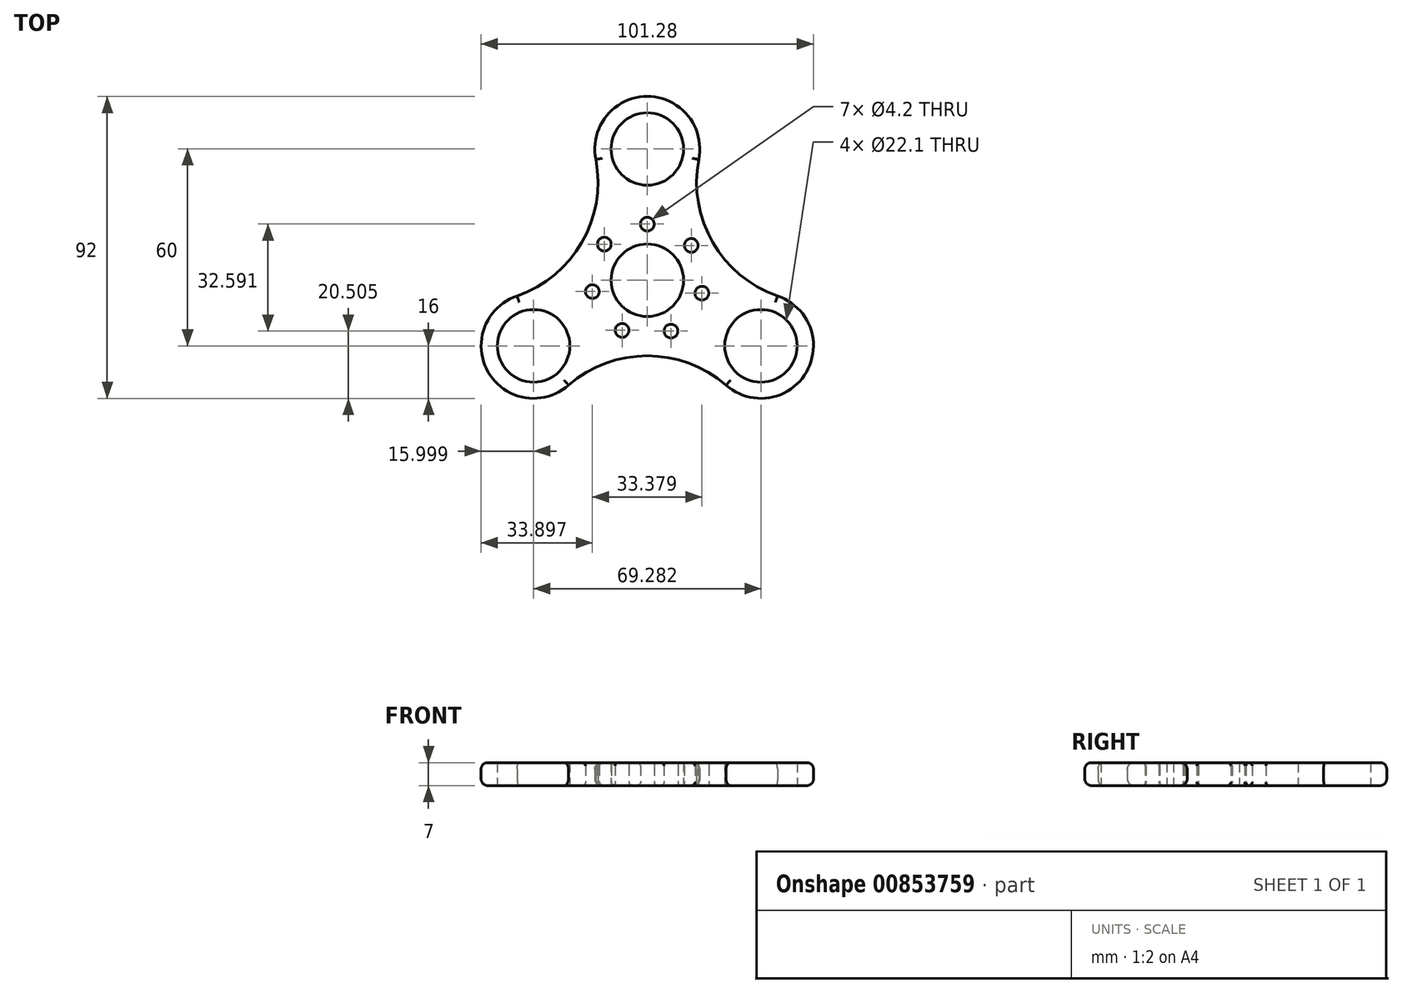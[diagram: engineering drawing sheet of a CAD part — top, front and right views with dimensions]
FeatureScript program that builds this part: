
annotation { "Feature Type Name" : "Feature", "Feature Type Description" : "" }
export const myFeature = defineFeature(function(context is Context, id is Id, definition is map)
    precondition{}
    {
        {
            var Q0;
            Q0=qCreatedBy(makeId("Top.planeOp"),FACE);
            var sketch = newSketch(context, id + "F0", { "sketchPlane" : qUnion([Q0])});
            skCircle(sketch, "E0", {"center": v(0, 0) * mm, "radius": 11.05 * mm});
            skCircle(sketch, "E1", {"center": v(0, 40) * mm, "radius": 11.05 * mm});
            skCircle(sketch, "E2.1.0", {"center": v(-34.64, -20) * mm, "radius": 11.05 * mm});
            skCircle(sketch, "E2.2.0", {"center": v(34.64, -20) * mm, "radius": 11.05 * mm});
            skCircle(sketch, "E3", {"center": v(0, 40) * mm, "radius": 16 * mm});
            skCircle(sketch, "E4.1.0", {"center": v(-34.64, -20) * mm, "radius": 16 * mm});
            skCircle(sketch, "E4.2.0", {"center": v(34.64, -20) * mm, "radius": 16 * mm});
            skLineSegment(sketch, "E5", {"start": v(0, 40) * mm, "end": v(34.64, -20) * mm, "construction": true});
            skLineSegment(sketch, "E6", {"start": v(14.06, 40) * mm, "end": v(43.8, -11.53) * mm, "construction": true});
            skArc(sketch, "E7", {"start": v(15.73, 37.1) * mm, "mid": v(19.95, 11.52) * mm, "end": v(40, -4.92) * mm});
            skArc(sketch, "E8.1.0", {"start": v(-40, -4.92) * mm, "mid": v(-19.95, 11.52) * mm, "end": v(-15.73, 37.1) * mm});
            skArc(sketch, "E8.2.0", {"start": v(24.26, -32.17) * mm, "mid": v(0, -23.04) * mm, "end": v(-24.26, -32.17) * mm});
            skCircle(sketch, "E9", {"center": v(0, 17.1) * mm, "radius": 2.1 * mm});
            skCircle(sketch, "E10.1.0", {"center": v(13.41, 10.6) * mm, "radius": 2.1 * mm});
            skCircle(sketch, "E10.2.0", {"center": v(16.64, -3.94) * mm, "radius": 2.1 * mm});
            skCircle(sketch, "E10.3.0", {"center": v(7.23, -15.5) * mm, "radius": 2.1 * mm});
            skCircle(sketch, "E10.4.0", {"center": v(-7.67, -15.28) * mm, "radius": 2.1 * mm});
            skCircle(sketch, "E10.5.0", {"center": v(-16.74, -3.46) * mm, "radius": 2.1 * mm});
            skCircle(sketch, "E10.6.0", {"center": v(-13.1, 10.99) * mm, "radius": 2.1 * mm});
            skLineSegment(sketch, "E10.anchor1", {"start": v(0, 0) * mm, "end": v(0, 17.1) * mm, "construction": true});
            skLineSegment(sketch, "E10.anchor2", {"start": v(0, 0) * mm, "end": v(-13.1, 10.99) * mm, "construction": true});
            skSolve(sketch);
        }
        {
            var Q0;
            Q0 = qSketchRegion(id + "F0", true);
            extrude(context, id + "F1", {"entities" : qUnion([Q0]), "depth" : 7 * mm, "offsetDistance" : 25 * mm});
        }
        {
            var Q0;
            Q0=makeQuery(id+"F1.opExtrude","CAP_EDGE",EDGE,{"disambiguationData":[OSD([sQuery(id+"F0.wireOp",EDGE,"E8.1.0")])],"isStart":false});
            var Q1;
            Q1=makeQuery(id+"F1.opExtrude","CAP_EDGE",EDGE,{"disambiguationData":[OSD([sQuery(id+"F0.wireOp",EDGE,"E7")])],"isStart":true});
            var Q2;
            Q2=makeQuery(id+"F1.opExtrude","CAP_EDGE",EDGE,{"disambiguationData":[OSD([sQuery(id+"F0.wireOp",EDGE,"E7")])],"isStart":false});
            var Q3;
            Q3=makeQuery(id+"F1.opExtrude","CAP_EDGE",EDGE,{"disambiguationData":[OSD([sQuery(id+"F0.wireOp",EDGE,"E8.2.0")])],"isStart":false});
            var Q4;
            Q4=makeQuery(id+"F1.opExtrude","CAP_EDGE",EDGE,{"disambiguationData":[OSD([sQuery(id+"F0.wireOp",EDGE,"E4.1.0")])],"isStart":false});
            var Q5;
            Q5=makeQuery(id+"F1.opExtrude","CAP_EDGE",EDGE,{"disambiguationData":[OSD([sQuery(id+"F0.wireOp",EDGE,"E4.2.0")])],"isStart":false});
            var Q6;
            Q6=makeQuery(id+"F1.opExtrude","CAP_EDGE",EDGE,{"disambiguationData":[OSD([sQuery(id+"F0.wireOp",EDGE,"E3")])],"isStart":false});
            var Q7;
            Q7=makeQuery(id+"F1.opExtrude","CAP_EDGE",EDGE,{"disambiguationData":[OSD([sQuery(id+"F0.wireOp",EDGE,"E3")])],"isStart":true});
            var Q8;
            Q8=makeQuery(id+"F1.opExtrude","CAP_EDGE",EDGE,{"disambiguationData":[OSD([sQuery(id+"F0.wireOp",EDGE,"E4.2.0")])],"isStart":true});
            var Q9;
            Q9=makeQuery(id+"F1.opExtrude","CAP_EDGE",EDGE,{"disambiguationData":[OSD([sQuery(id+"F0.wireOp",EDGE,"E8.1.0")])],"isStart":true});
            var Q10;
            Q10=makeQuery(id+"F1.opExtrude","CAP_EDGE",EDGE,{"disambiguationData":[OSD([sQuery(id+"F0.wireOp",EDGE,"E4.1.0")])],"isStart":true});
            fillet(context, id + "F2", {"entities" : qUnion([Q0, Q1, Q2, Q3, Q4, Q5, Q6, Q7, Q8, Q9, Q10]), "radius" : 2 * mm, "tangentPropagation" : true, "allowEdgeOverflow" : false});
        }
        {
            var Q0;
            Q0=makeQuery(id+"F1.opExtrude","CAP_EDGE",EDGE,{"disambiguationData":[OSD([sQuery(id+"F0.wireOp",EDGE,"E9")])],"isStart":false});
            var Q1;
            Q1=makeQuery(id+"F1.opExtrude","CAP_EDGE",EDGE,{"disambiguationData":[OSD([sQuery(id+"F0.wireOp",EDGE,"E10.6.0")])],"isStart":false});
            var Q2;
            Q2=makeQuery(id+"F1.opExtrude","CAP_EDGE",EDGE,{"disambiguationData":[OSD([sQuery(id+"F0.wireOp",EDGE,"E10.5.0")])],"isStart":false});
            var Q3;
            Q3=makeQuery(id+"F1.opExtrude","CAP_EDGE",EDGE,{"disambiguationData":[OSD([sQuery(id+"F0.wireOp",EDGE,"E10.4.0")])],"isStart":false});
            var Q4;
            Q4=makeQuery(id+"F1.opExtrude","CAP_EDGE",EDGE,{"disambiguationData":[OSD([sQuery(id+"F0.wireOp",EDGE,"E10.3.0")])],"isStart":false});
            var Q5;
            Q5=makeQuery(id+"F1.opExtrude","CAP_EDGE",EDGE,{"disambiguationData":[OSD([sQuery(id+"F0.wireOp",EDGE,"E10.2.0")])],"isStart":false});
            var Q6;
            Q6=makeQuery(id+"F1.opExtrude","CAP_EDGE",EDGE,{"disambiguationData":[OSD([sQuery(id+"F0.wireOp",EDGE,"E10.1.0")])],"isStart":false});
            var Q7;
            Q7=makeQuery(id+"F1.opExtrude","CAP_EDGE",EDGE,{"disambiguationData":[OSD([sQuery(id+"F0.wireOp",EDGE,"E10.4.0")])],"isStart":true});
            var Q8;
            Q8=makeQuery(id+"F1.opExtrude","CAP_EDGE",EDGE,{"disambiguationData":[OSD([sQuery(id+"F0.wireOp",EDGE,"E10.5.0")])],"isStart":true});
            var Q9;
            Q9=makeQuery(id+"F1.opExtrude","CAP_EDGE",EDGE,{"disambiguationData":[OSD([sQuery(id+"F0.wireOp",EDGE,"E10.6.0")])],"isStart":true});
            var Q10;
            Q10=makeQuery(id+"F1.opExtrude","CAP_EDGE",EDGE,{"disambiguationData":[OSD([sQuery(id+"F0.wireOp",EDGE,"E9")])],"isStart":true});
            var Q11;
            Q11=makeQuery(id+"F1.opExtrude","CAP_EDGE",EDGE,{"disambiguationData":[OSD([sQuery(id+"F0.wireOp",EDGE,"E10.1.0")])],"isStart":true});
            var Q12;
            Q12=makeQuery(id+"F1.opExtrude","CAP_EDGE",EDGE,{"disambiguationData":[OSD([sQuery(id+"F0.wireOp",EDGE,"E10.2.0")])],"isStart":true});
            var Q13;
            Q13=makeQuery(id+"F1.opExtrude","CAP_EDGE",EDGE,{"disambiguationData":[OSD([sQuery(id+"F0.wireOp",EDGE,"E10.3.0")])],"isStart":true});
            fillet(context, id + "F3", {"entities" : qUnion([Q0, Q1, Q2, Q3, Q4, Q5, Q6, Q7, Q8, Q9, Q10, Q11, Q12, Q13]), "radius" : 1 * mm, "tangentPropagation" : true, "allowEdgeOverflow" : false});
        }
    });
